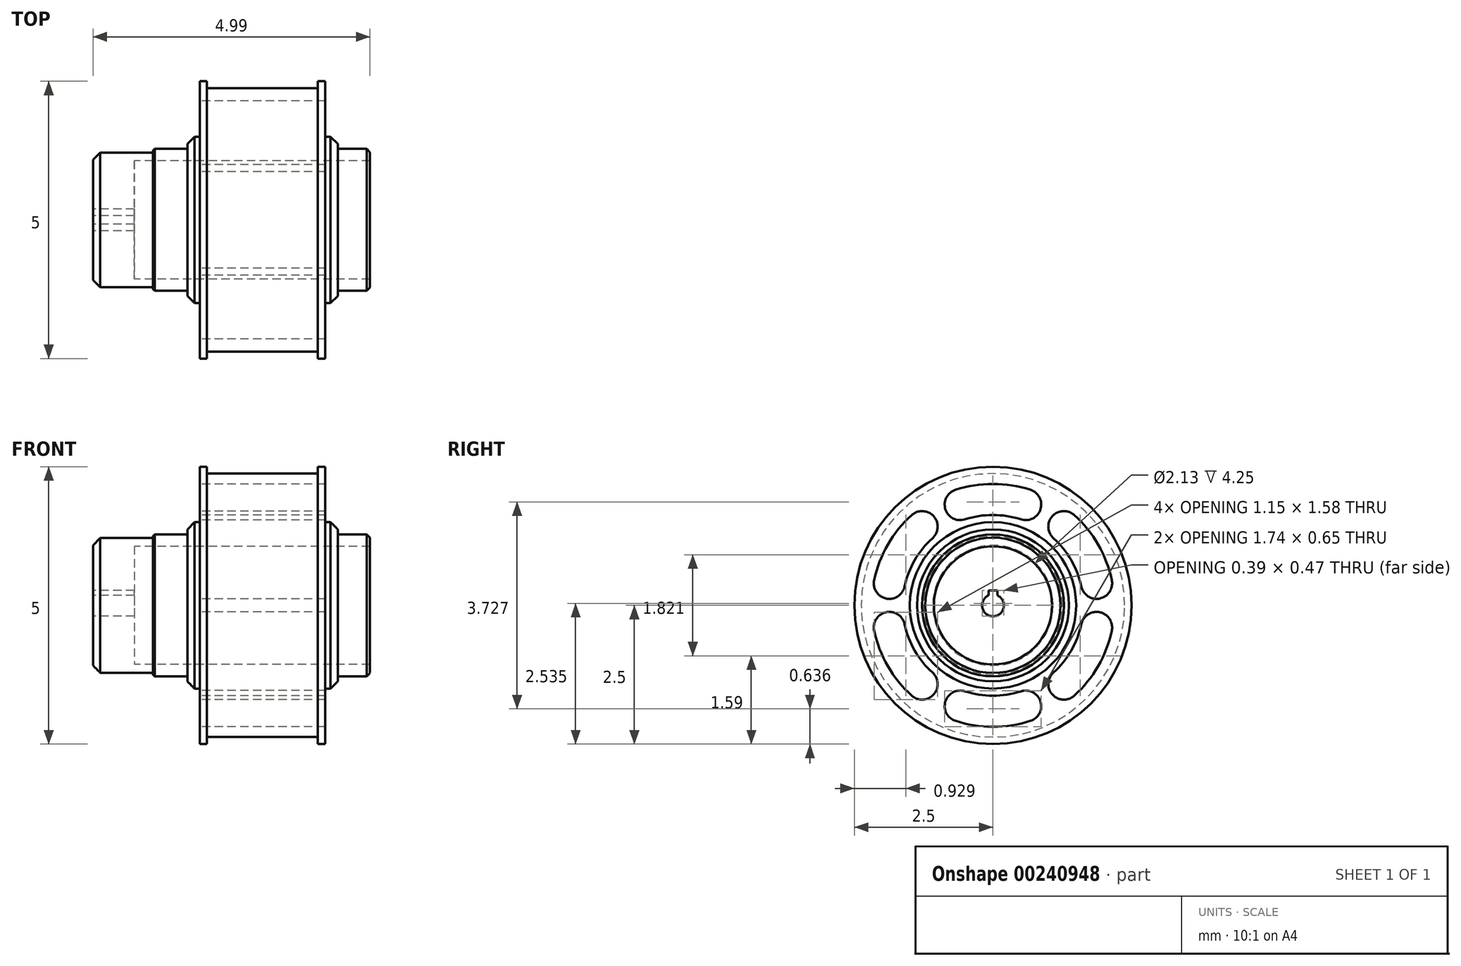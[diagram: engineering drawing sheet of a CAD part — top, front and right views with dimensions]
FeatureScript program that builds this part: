
annotation { "Feature Type Name" : "Feature", "Feature Type Description" : "" }
export const myFeature = defineFeature(function(context is Context, id is Id, definition is map)
    precondition{}
    {
        {
            var Q0;
            Q0=qCreatedBy(makeId("Top.planeOp"),FACE);
            var sketch = newSketch(context, id + "F0", { "sketchPlane" : qUnion([Q0])});
            skLineSegment(sketch, "E0", {"start": v(-29.2, 1.07) * mm, "end": v(-29.2, 1.28) * mm});
            skLineSegment(sketch, "E1", {"start": v(-29.2, 1.28) * mm, "end": v(-29.78, 1.28) * mm});
            skLineSegment(sketch, "E2", {"start": v(-29.78, 1.28) * mm, "end": v(-29.78, 1.5) * mm});
            skLineSegment(sketch, "E3", {"start": v(-29.78, 1.5) * mm, "end": v(-30, 1.5) * mm});
            skLineSegment(sketch, "E4", {"start": v(-30, 1.5) * mm, "end": v(-30, 2.5) * mm});
            skLineSegment(sketch, "E5", {"start": v(-30, 2.5) * mm, "end": v(-30.14, 2.5) * mm});
            skLineSegment(sketch, "E6", {"start": v(-30.14, 2.5) * mm, "end": v(-30.14, 2.38) * mm});
            skLineSegment(sketch, "E7", {"start": v(-30.14, 2.38) * mm, "end": v(-32.14, 2.38) * mm});
            skLineSegment(sketch, "E8", {"start": v(-32.14, 2.38) * mm, "end": v(-32.14, 2.5) * mm});
            skLineSegment(sketch, "E9", {"start": v(-32.14, 2.5) * mm, "end": v(-32.27, 2.5) * mm});
            skLineSegment(sketch, "E10", {"start": v(-32.27, 2.5) * mm, "end": v(-32.27, 1.5) * mm});
            skLineSegment(sketch, "E11", {"start": v(-32.27, 1.5) * mm, "end": v(-32.5, 1.5) * mm});
            skLineSegment(sketch, "E12", {"start": v(-32.5, 1.5) * mm, "end": v(-32.5, 1.28) * mm});
            skLineSegment(sketch, "E13", {"start": v(-32.5, 1.28) * mm, "end": v(-33.11, 1.28) * mm});
            skLineSegment(sketch, "E14", {"start": v(-33.11, 1.28) * mm, "end": v(-33.11, 1.21) * mm});
            skLineSegment(sketch, "E15", {"start": v(-34.2, 1.21) * mm, "end": v(-34.2, 0) * mm});
            skLineSegment(sketch, "E16", {"start": v(-34.2, 0) * mm, "end": v(-33.45, 0) * mm});
            skLineSegment(sketch, "E17", {"start": v(-34.2, 1.21) * mm, "end": v(-33.11, 1.21) * mm});
            skLineSegment(sketch, "E18", {"start": v(-29.2, 1.07) * mm, "end": v(-33.45, 1.07) * mm});
            skLineSegment(sketch, "E19", {"start": v(-33.45, 1.07) * mm, "end": v(-33.45, 0) * mm});
            skPoint(sketch, "E20.orphan", {"position": v(-29.2, 0) * mm});
            skSolve(sketch);
        }
        {
            var Q0;
            Q0 = qSketchRegion(id + "F0", true);
            var Q1;
            Q1=sQuery(id+"F0.wireOp",EDGE,"E16");
            revolve(context, id + "F1", {"entities" : qUnion([Q0]), "axis" : qUnion([Q1]), "revolveType" : RevolveType.FULL});
        }
        {
            var Q0;
            Q0=makeQuery(id+"F1.opRevolve","SWEPT_FACE",FACE,{"disambiguationData":[OSD([sQuery(id+"F0.wireOp",EDGE,"E15")])]});
            var sketch = newSketch(context, id + "F2", { "sketchPlane" : qUnion([Q0])});
            skArc(sketch, "E21", {"start": v(-0.08, 0.18) * mm, "mid": v(0, -0.2) * mm, "end": v(0.08, 0.18) * mm});
            skLineSegment(sketch, "E22", {"start": v(0, 0.27) * mm, "end": v(0.08, 0.27) * mm});
            skLineSegment(sketch, "E23", {"start": v(0, 0.27) * mm, "end": v(-0.08, 0.27) * mm});
            skLineSegment(sketch, "E24", {"start": v(-0.08, 0.27) * mm, "end": v(-0.08, 0.18) * mm});
            skLineSegment(sketch, "E25", {"start": v(0.08, 0.27) * mm, "end": v(0.08, 0.18) * mm});
            skSolve(sketch);
        }
        {
            var Q0;
            Q0 = qSketchRegion(id + "F2", true);
            extrude(context, id + "F3", {"entities" : qUnion([Q0]), "operationType" : NewBodyOperationType.REMOVE, "oppositeDirection" : true, "depth" : 6.86 * mm});
        }
        {
            var Q0;
            Q0=makeQuery(id+"F1.opRevolve","SWEPT_EDGE",EDGE,{"disambiguationData":[OSD([sQuery(id+"F0.wireOp",EDGE,"E15"),sQuery(id+"F0.wireOp",EDGE,"E17")])]});
            var Q1;
            Q1=makeQuery(id+"F1.opRevolve","SWEPT_EDGE",EDGE,{"disambiguationData":[OSD([sQuery(id+"F0.wireOp",EDGE,"E11"),sQuery(id+"F0.wireOp",EDGE,"E12")])]});
            var Q2;
            Q2=makeQuery(id+"F1.opRevolve","SWEPT_EDGE",EDGE,{"disambiguationData":[OSD([sQuery(id+"F0.wireOp",EDGE,"E2"),sQuery(id+"F0.wireOp",EDGE,"E3")])]});
            chamfer(context, id + "F4", {"entities" : qUnion([Q0, Q1, Q2]), "width" : 0.13 * mm, "tangentPropagation" : true});
        }
        {
            var Q0;
            Q0=makeQuery(id+"F1.opRevolve","SWEPT_EDGE",EDGE,{"disambiguationData":[OSD([sQuery(id+"F0.wireOp",EDGE,"E0"),sQuery(id+"F0.wireOp",EDGE,"E1")])]});
            chamfer(context, id + "F5", {"entities" : qUnion([Q0]), "width" : 0.06 * mm, "tangentPropagation" : true});
        }
        {
            var Q0;
            Q0=makeQuery(id+"F1.opRevolve","SWEPT_EDGE",EDGE,{"disambiguationData":[OSD([sQuery(id+"F0.wireOp",EDGE,"E13"),sQuery(id+"F0.wireOp",EDGE,"E14")])]});
            chamfer(context, id + "F6", {"entities" : qUnion([Q0]), "width" : 0.03 * mm, "tangentPropagation" : true});
        }
        {
            var Q0;
            Q0=makeQuery(id+"F1.opRevolve","SWEPT_FACE",FACE,{"disambiguationData":[OSD([sQuery(id+"F0.wireOp",EDGE,"E10")])]});
            var sketch = newSketch(context, id + "F7", { "sketchPlane" : qUnion([Q0])});
            skArc(sketch, "E26", {"start": v(0.5, 1.55) * mm, "mid": v(0.86, 1.73) * mm, "end": v(0.68, 2.08) * mm});
            skArc(sketch, "E27", {"start": v(-0.68, 2.08) * mm, "mid": v(-0.86, 1.73) * mm, "end": v(-0.5, 1.55) * mm});
            skArc(sketch, "E28", {"start": v(0.5, 1.55) * mm, "mid": v(0, 1.63) * mm, "end": v(-0.5, 1.55) * mm});
            skArc(sketch, "E29", {"start": v(0.68, 2.08) * mm, "mid": v(0, 2.19) * mm, "end": v(-0.68, 2.08) * mm});
            skArc(sketch, "E30.1.0", {"start": v(-1.1, 1.21) * mm, "mid": v(-1.07, 1.6) * mm, "end": v(-1.47, 1.63) * mm});
            skArc(sketch, "E30.1.1", {"start": v(-1.47, 1.63) * mm, "mid": v(-1.9, 1.1) * mm, "end": v(-2.14, 0.46) * mm});
            skArc(sketch, "E30.1.2", {"start": v(-2.14, 0.46) * mm, "mid": v(-1.93, 0.12) * mm, "end": v(-1.6, 0.34) * mm});
            skArc(sketch, "E30.1.3", {"start": v(-1.1, 1.21) * mm, "mid": v(-1.41, 0.82) * mm, "end": v(-1.6, 0.34) * mm});
            skArc(sketch, "E30.2.0", {"start": v(-1.6, -0.34) * mm, "mid": v(-1.93, -0.12) * mm, "end": v(-2.14, -0.46) * mm});
            skArc(sketch, "E30.2.1", {"start": v(-2.14, -0.46) * mm, "mid": v(-1.9, -1.1) * mm, "end": v(-1.47, -1.63) * mm});
            skArc(sketch, "E30.2.2", {"start": v(-1.47, -1.63) * mm, "mid": v(-1.07, -1.6) * mm, "end": v(-1.1, -1.21) * mm});
            skArc(sketch, "E30.2.3", {"start": v(-1.6, -0.34) * mm, "mid": v(-1.41, -0.81) * mm, "end": v(-1.1, -1.21) * mm});
            skArc(sketch, "E30.3.0", {"start": v(-0.5, -1.55) * mm, "mid": v(-0.86, -1.73) * mm, "end": v(-0.68, -2.08) * mm});
            skArc(sketch, "E30.3.1", {"start": v(-0.68, -2.08) * mm, "mid": v(0, -2.19) * mm, "end": v(0.68, -2.08) * mm});
            skArc(sketch, "E30.3.2", {"start": v(0.68, -2.08) * mm, "mid": v(0.86, -1.73) * mm, "end": v(0.5, -1.55) * mm});
            skArc(sketch, "E30.3.3", {"start": v(-0.5, -1.55) * mm, "mid": v(0, -1.63) * mm, "end": v(0.5, -1.55) * mm});
            skArc(sketch, "E30.4.0", {"start": v(1.1, -1.21) * mm, "mid": v(1.07, -1.6) * mm, "end": v(1.47, -1.63) * mm});
            skArc(sketch, "E30.4.1", {"start": v(1.47, -1.63) * mm, "mid": v(1.9, -1.1) * mm, "end": v(2.14, -0.46) * mm});
            skArc(sketch, "E30.4.2", {"start": v(2.14, -0.46) * mm, "mid": v(1.93, -0.12) * mm, "end": v(1.6, -0.34) * mm});
            skArc(sketch, "E30.4.3", {"start": v(1.1, -1.21) * mm, "mid": v(1.41, -0.82) * mm, "end": v(1.6, -0.34) * mm});
            skArc(sketch, "E30.5.0", {"start": v(1.6, 0.34) * mm, "mid": v(1.93, 0.12) * mm, "end": v(2.14, 0.46) * mm});
            skArc(sketch, "E30.5.1", {"start": v(2.14, 0.46) * mm, "mid": v(1.9, 1.1) * mm, "end": v(1.47, 1.63) * mm});
            skArc(sketch, "E30.5.2", {"start": v(1.47, 1.63) * mm, "mid": v(1.07, 1.6) * mm, "end": v(1.1, 1.21) * mm});
            skArc(sketch, "E30.5.3", {"start": v(1.6, 0.34) * mm, "mid": v(1.41, 0.82) * mm, "end": v(1.1, 1.21) * mm});
            skSolve(sketch);
        }
        {
            var Q0;
            Q0=makeQuery(id+"F7.imprint","IMPRINT",FACE,{"disambiguationData":[TD([[makeQuery(id+"F7.imprint","IMPRINT",EDGE,{"derivedFrom":sQuery(id+"F7.wireOp",EDGE,"E26")}),1.0]])]});
            var Q1;
            Q1=makeQuery(id+"F7.imprint","IMPRINT",FACE,{"disambiguationData":[TD([[makeQuery(id+"F7.imprint","IMPRINT",EDGE,{"derivedFrom":sQuery(id+"F7.wireOp",EDGE,"E30.1.0")}),1.0]])]});
            var Q2;
            Q2=makeQuery(id+"F7.imprint","IMPRINT",FACE,{"disambiguationData":[TD([[makeQuery(id+"F7.imprint","IMPRINT",EDGE,{"derivedFrom":sQuery(id+"F7.wireOp",EDGE,"E30.2.0")}),1.0]])]});
            var Q3;
            Q3=makeQuery(id+"F7.imprint","IMPRINT",FACE,{"disambiguationData":[TD([[makeQuery(id+"F7.imprint","IMPRINT",EDGE,{"derivedFrom":sQuery(id+"F7.wireOp",EDGE,"E30.3.0")}),1.0]])]});
            var Q4;
            Q4=makeQuery(id+"F7.imprint","IMPRINT",FACE,{"disambiguationData":[TD([[makeQuery(id+"F7.imprint","IMPRINT",EDGE,{"derivedFrom":sQuery(id+"F7.wireOp",EDGE,"E30.4.0")}),1.0]])]});
            var Q5;
            Q5=makeQuery(id+"F7.imprint","IMPRINT",FACE,{"disambiguationData":[TD([[makeQuery(id+"F7.imprint","IMPRINT",EDGE,{"derivedFrom":sQuery(id+"F7.wireOp",EDGE,"E30.5.0")}),1.0]])]});
            extrude(context, id + "F8", {"entities" : qUnion([Q0, Q1, Q2, Q3, Q4, Q5]), "operationType" : NewBodyOperationType.REMOVE, "oppositeDirection" : true, "depth" : 6.8 * mm});
        }
        {
            var Q0;
            Q0=makeQuery(id+"F1.opRevolve","SWEPT_FACE",FACE,{"disambiguationData":[OSD([sQuery(id+"F0.wireOp",EDGE,"E10")])]});
            var sketch = newSketch(context, id + "F9", { "sketchPlane" : qUnion([Q0])});
            skArc(sketch, "E31", {"start": v(-1.1, 1.21) * mm, "mid": v(-1.41, 0.81) * mm, "end": v(-1.6, 0.34) * mm});
            skArc(sketch, "E32", {"start": v(-1.47, 1.63) * mm, "mid": v(-1.9, 1.1) * mm, "end": v(-2.14, 0.46) * mm});
            skPoint(sketch, "E33", {"position": v(1.28, 1.42) * mm});
            skPoint(sketch, "E34", {"position": v(0.6, 1.82) * mm});
            skPoint(sketch, "E35", {"position": v(1.87, 0.4) * mm});
            skPoint(sketch, "E36", {"position": v(1.87, -0.4) * mm});
            skPoint(sketch, "E37", {"position": v(1.28, -1.42) * mm});
            skPoint(sketch, "E38", {"position": v(0.6, -1.82) * mm});
            skPoint(sketch, "E39", {"position": v(-0.6, -1.82) * mm});
            skPoint(sketch, "E40", {"position": v(-1.28, -1.42) * mm});
            skPoint(sketch, "E41", {"position": v(-1.87, 0.4) * mm});
            skPoint(sketch, "E42", {"position": v(-0.6, 1.82) * mm});
            skPoint(sketch, "E43", {"position": v(-1.28, 1.42) * mm});
            skPoint(sketch, "E44", {"position": v(-1.87, -0.4) * mm});
            skArc(sketch, "E45", {"start": v(0.5, 1.55) * mm, "mid": v(0.86, 1.73) * mm, "end": v(0.68, 2.08) * mm});
            skArc(sketch, "E46", {"start": v(1.47, 1.63) * mm, "mid": v(1.07, 1.6) * mm, "end": v(1.1, 1.21) * mm});
            skArc(sketch, "E47", {"start": v(1.6, 0.34) * mm, "mid": v(1.93, 0.12) * mm, "end": v(2.14, 0.46) * mm});
            skArc(sketch, "E48", {"start": v(2.14, -0.46) * mm, "mid": v(1.93, -0.12) * mm, "end": v(1.6, -0.34) * mm});
            skArc(sketch, "E49", {"start": v(1.1, -1.21) * mm, "mid": v(1.07, -1.6) * mm, "end": v(1.47, -1.63) * mm});
            skArc(sketch, "E50", {"start": v(0.68, -2.08) * mm, "mid": v(0.86, -1.73) * mm, "end": v(0.5, -1.55) * mm});
            skArc(sketch, "E51", {"start": v(-0.5, -1.55) * mm, "mid": v(-0.86, -1.73) * mm, "end": v(-0.68, -2.08) * mm});
            skArc(sketch, "E52", {"start": v(-1.47, -1.63) * mm, "mid": v(-1.07, -1.6) * mm, "end": v(-1.1, -1.21) * mm});
            skArc(sketch, "E53", {"start": v(-1.6, -0.34) * mm, "mid": v(-1.93, -0.12) * mm, "end": v(-2.14, -0.46) * mm});
            skArc(sketch, "E54", {"start": v(-2.14, 0.46) * mm, "mid": v(-1.93, 0.12) * mm, "end": v(-1.6, 0.34) * mm});
            skArc(sketch, "E55", {"start": v(-1.1, 1.21) * mm, "mid": v(-1.07, 1.6) * mm, "end": v(-1.47, 1.63) * mm});
            skArc(sketch, "E56", {"start": v(-0.68, 2.08) * mm, "mid": v(-0.86, 1.73) * mm, "end": v(-0.5, 1.55) * mm});
            skArc(sketch, "E57.trimOffspring", {"start": v(0.68, 2.08) * mm, "mid": v(0, 2.19) * mm, "end": v(-0.68, 2.08) * mm});
            skArc(sketch, "E58.trimOffspring", {"start": v(0.5, 1.55) * mm, "mid": v(0, 1.63) * mm, "end": v(-0.5, 1.55) * mm});
            skArc(sketch, "E59.trimOffspring", {"start": v(1.6, 0.34) * mm, "mid": v(1.41, 0.81) * mm, "end": v(1.1, 1.21) * mm});
            skArc(sketch, "E60.trimOffspring", {"start": v(2.14, 0.46) * mm, "mid": v(1.9, 1.1) * mm, "end": v(1.47, 1.63) * mm});
            skArc(sketch, "E61.trimOffspring", {"start": v(1.1, -1.21) * mm, "mid": v(1.41, -0.81) * mm, "end": v(1.6, -0.34) * mm});
            skArc(sketch, "E62.trimOffspring", {"start": v(1.47, -1.63) * mm, "mid": v(1.9, -1.1) * mm, "end": v(2.14, -0.46) * mm});
            skArc(sketch, "E63.trimOffspring", {"start": v(-0.68, -2.08) * mm, "mid": v(0, -2.19) * mm, "end": v(0.68, -2.08) * mm});
            skArc(sketch, "E64.trimOffspring", {"start": v(-0.5, -1.55) * mm, "mid": v(0, -1.63) * mm, "end": v(0.5, -1.55) * mm});
            skArc(sketch, "E65.trimOffspring", {"start": v(-2.14, -0.46) * mm, "mid": v(-1.9, -1.1) * mm, "end": v(-1.47, -1.63) * mm});
            skArc(sketch, "E66.trimOffspring", {"start": v(-1.6, -0.34) * mm, "mid": v(-1.41, -0.82) * mm, "end": v(-1.1, -1.21) * mm});
            skSolve(sketch);
        }
        {
            var Q0;
            Q0=makeQuery(id+"F9.imprint","IMPRINT",FACE,{"disambiguationData":[TD([[makeQuery(id+"F9.imprint","IMPRINT",EDGE,{"derivedFrom":sQuery(id+"F9.wireOp",EDGE,"E31")}),-1.0]])]});
            var Q1;
            Q1=makeQuery(id+"F9.imprint","IMPRINT",FACE,{"disambiguationData":[TD([[makeQuery(id+"F9.imprint","IMPRINT",EDGE,{"derivedFrom":sQuery(id+"F9.wireOp",EDGE,"E52")}),1.0]])]});
            var Q2;
            Q2=makeQuery(id+"F9.imprint","IMPRINT",FACE,{"disambiguationData":[TD([[makeQuery(id+"F9.imprint","IMPRINT",EDGE,{"derivedFrom":sQuery(id+"F9.wireOp",EDGE,"E50")}),1.0]])]});
            var Q3;
            Q3=makeQuery(id+"F9.imprint","IMPRINT",FACE,{"disambiguationData":[TD([[makeQuery(id+"F9.imprint","IMPRINT",EDGE,{"derivedFrom":sQuery(id+"F9.wireOp",EDGE,"E48")}),1.0]])]});
            var Q4;
            Q4=makeQuery(id+"F9.imprint","IMPRINT",FACE,{"disambiguationData":[TD([[makeQuery(id+"F9.imprint","IMPRINT",EDGE,{"derivedFrom":sQuery(id+"F9.wireOp",EDGE,"E46")}),1.0]])]});
            var Q5;
            Q5=makeQuery(id+"F9.imprint","IMPRINT",FACE,{"disambiguationData":[TD([[makeQuery(id+"F9.imprint","IMPRINT",EDGE,{"derivedFrom":sQuery(id+"F9.wireOp",EDGE,"E45")}),1.0]])]});
            extrude(context, id + "F10", {"entities" : qUnion([Q0, Q1, Q2, Q3, Q4, Q5]), "operationType" : NewBodyOperationType.REMOVE, "oppositeDirection" : true, "depth" : 14.1 * mm});
        }
    });
